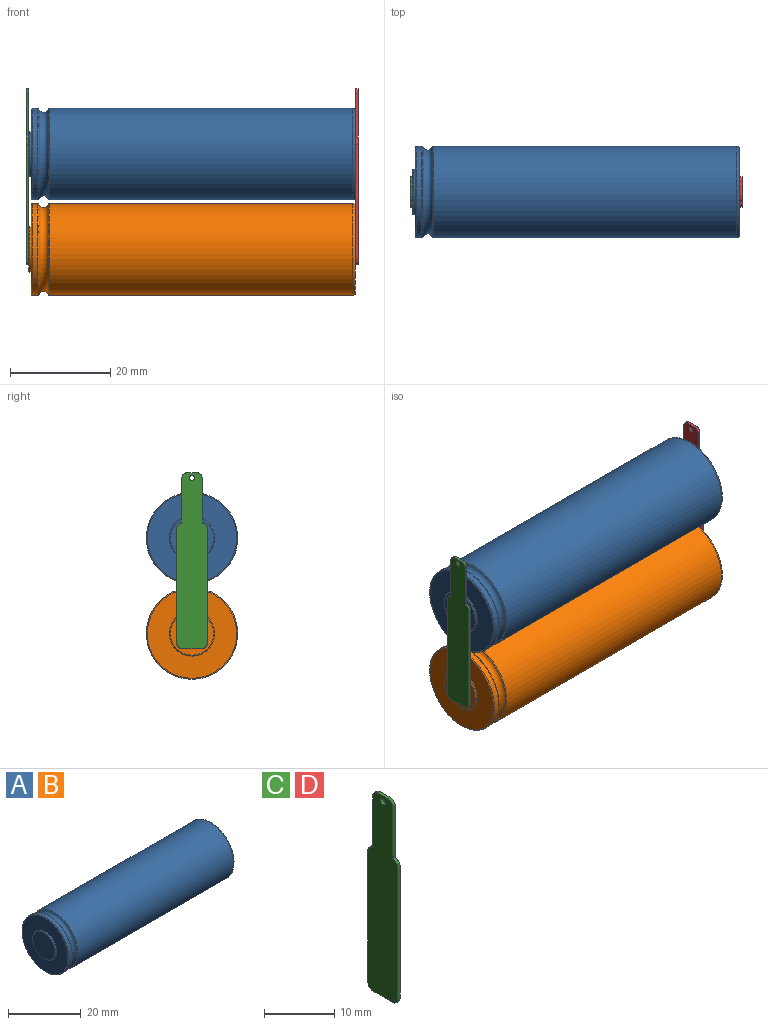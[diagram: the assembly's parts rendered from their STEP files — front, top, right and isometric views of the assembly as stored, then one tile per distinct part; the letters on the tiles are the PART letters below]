
ASSEMBLY  parts=4 mates=3
PART A: 12 faces, bbox 65.1x20.2x20.2 mm
  f0: torus R=9.32mm, axis (1,0,0), area 130.7mm2, adj f1,f11
  f1: torus R=8.9mm, axis (1,0,0), area 13.9mm2, adj f0,f2
  f2: cylinder r=9.1mm len=18.2mm, axis (1,0,0), area 67.1mm2, adj f1,f3
  f3: torus R=8.9mm, axis (1,0,0), area 17.8mm2, adj f2,f4
  f4: plane 17.8x17.8mm, normal (-1,0,0), area 185.2mm2, adj f3,f5
  f5: cylinder r=4.5mm len=9mm, axis (1,0,0), area 8.5mm2, adj f4,f6
  f6: torus R=4.3mm, axis (1,0,0), area 8.7mm2, adj f5,f7
  f7: plane 8.6x8.6mm, normal (-1,0,0), area 58.1mm2, adj f6
  f8: plane 17.2x17.2mm, normal (1,0,0), area 232.4mm2, adj f9
  f9: torus R=8.6mm, axis (1,0,0), area 44mm2, adj f8,f10
  f10: cylinder r=9.1mm len=60.47mm, axis (1,0,0), area 3457.7mm2, adj f9,f11
  f11: torus R=8.9mm, axis (1,0,0), area 13.9mm2, adj f0,f10
PART B: same geometry as A
PART C: 15 faces, bbox 0.5x6x35 mm
  f0: plane 2x0.5mm, normal (0,0,1), area 1mm2, adj f1,f12,f13,f14
  f1: cylinder r=1mm len=1mm, axis (-1,0,0), area 0.8mm2, adj f0,f2,f13,f14
  f2: plane 9x0.5mm, normal (0,-1,0), area 4.5mm2, adj f1,f3,f13,f14
  f3: cylinder r=1mm len=1mm, axis (-1,0,0), area 0.8mm2, adj f2,f4,f13,f14
  f4: plane 23x0.5mm, normal (0,-1,0), area 11.5mm2, adj f3,f5,f13,f14
  f5: cylinder r=1mm len=1mm, axis (-1,0,0), area 0.8mm2, adj f4,f6,f13,f14
  f6: plane 4x0.5mm, normal (0,0,-1), area 2mm2, adj f5,f7,f13,f14
  f7: cylinder r=1mm len=1mm, axis (-1,0,0), area 0.8mm2, adj f6,f8,f13,f14
  f8: plane 23x0.5mm, normal (0,1,0), area 11.5mm2, adj f7,f9,f13,f14
  f9: cylinder r=1mm len=1mm, axis (-1,0,0), area 0.8mm2, adj f8,f10,f13,f14
  f10: plane 9x0.5mm, normal (0,1,0), area 4.5mm2, adj f9,f12,f13,f14
  f11: cylinder r=0.5mm len=1mm, axis (-1,0,0), area 1.6mm2, adj f13,f14
  f12: cylinder r=1mm len=1mm, axis (-1,0,0), area 0.8mm2, adj f0,f10,f13,f14
  f13: plane 35x6mm, normal (1,0,0), area 187.9mm2, adj f0,f1,f2,f3,f4,f5,f6,f7
  f14: plane 35x6mm, normal (-1,0,0), area 187.9mm2, adj f0,f1,f2,f3,f4,f5,f6,f7
PART D: same geometry as C
PLACE A t=(32.65,0,19)mm
PLACE B t=(32.65,0,0)mm
PLACE C t=(-0.5,0,0)mm
PLACE D t=(65.1,0,0)mm
MATE fastened D.f14 <-> B.f0  axis (1,0,0) through (65.1,0,0)mm
MATE fastened C.f14 <-> B.f0  axis (1,0,0) through (-0.5,0,0)mm
MATE fastened B.f0 <-> A.f4  axis (-1,0,0) through (0.5,0,0)mm
